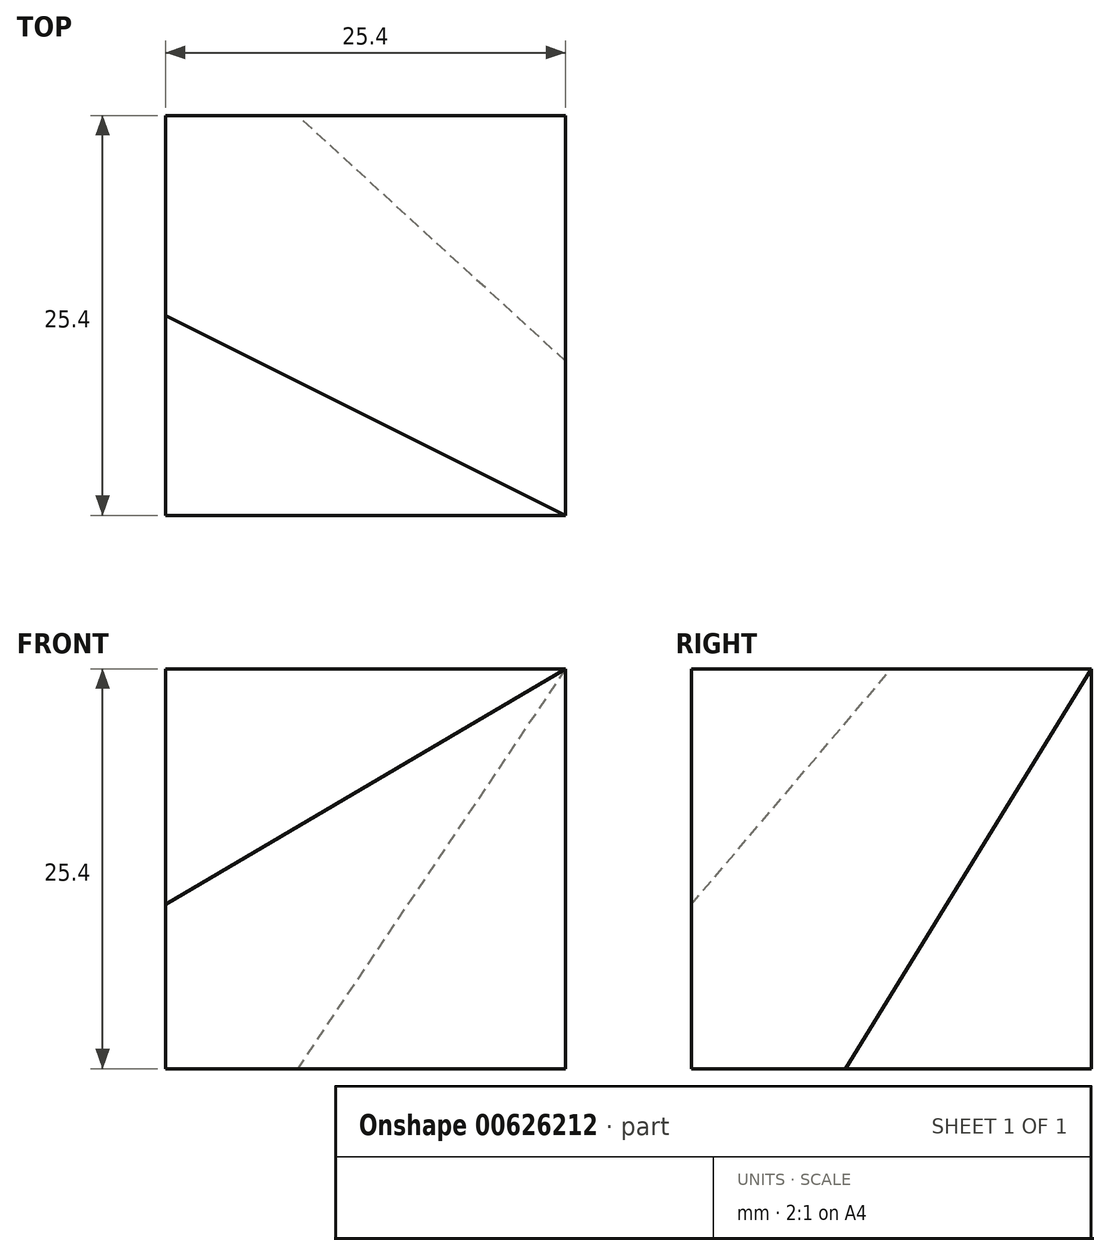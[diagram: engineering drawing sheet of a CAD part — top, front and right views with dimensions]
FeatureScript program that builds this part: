
annotation { "Feature Type Name" : "Feature", "Feature Type Description" : "" }
export const myFeature = defineFeature(function(context is Context, id is Id, definition is map)
    precondition{}
    {
        {
            var Q0;
            Q0=qCreatedBy(makeId("Top.planeOp"),FACE);
            var sketch = newSketch(context, id + "F0", { "sketchPlane" : qUnion([Q0])});
            skLineSegment(sketch, "E0.bottom", {"start": v(-12.7, 12.7) * mm, "end": v(12.7, 12.7) * mm});
            skLineSegment(sketch, "E0.top", {"start": v(-12.7, -12.7) * mm, "end": v(12.7, -12.7) * mm});
            skLineSegment(sketch, "E0.left", {"start": v(-12.7, 12.7) * mm, "end": v(-12.7, -12.7) * mm});
            skLineSegment(sketch, "E0.right", {"start": v(12.7, 12.7) * mm, "end": v(12.7, -12.7) * mm});
            skPoint(sketch, "E0.middle", {"position": v(0, 0) * mm});
            skSolve(sketch);
        }
        {
            var Q0;
            Q0 = qSketchRegion(id + "F0", true);
            extrude(context, id + "F1", {"entities" : qUnion([Q0]), "depth" : 25.4 * mm, "offsetDistance" : 25.4 * mm});
        }
        {
            var Q0;
            Q0=makeQuery(id+"F1.opExtrude","SWEPT_FACE",FACE,{"disambiguationData":[OSD([sQuery(id+"F0.wireOp",EDGE,"E0.left")])]});
            var sketch = newSketch(context, id + "F2", { "sketchPlane" : qUnion([Q0])});
            skLineSegment(sketch, "E1", {"start": v(-3.1, 25.4) * mm, "end": v(12.7, 10.44) * mm});
            skSolve(sketch);
        }
        {
            var Q0;
            Q0=makeQuery(id+"F1.opExtrude","CAP_EDGE",EDGE,{"disambiguationData":[OSD([sQuery(id+"F0.wireOp",EDGE,"E0.left")])],"isStart":false});
            cPoint(context, id + "F3", {"entities" : qUnion([Q0]), "parameter" : 0.5});
        }
        {
            var Q0;
            Q0 = qCreatedBy(id + "F3" ,VERTEX);
            var Q1;
            Q1=sQuery(id+"F2.wireOp",VERTEX,"E1.end");
            var Q2;
            Q2=makeQuery(id+"F1.opExtrude","CAP_VERTEX",VERTEX,{"disambiguationData":[OSD([sQuery(id+"F0.wireOp",EDGE,"E0.top"),sQuery(id+"F0.wireOp",EDGE,"E0.right")])],"isStart":false});
            cPlane(context, id + "F4", {"entities" : qUnion([Q0, Q1, Q2]), "cplaneType" : CPlaneType.THREE_POINT, "offset" : 25.4 * mm, "width" : 152.4 * mm, "height" : 152.4 * mm});
        }
        {
            var Q0;
            Q0=qCreatedBy(id+"F4.planeOp",FACE);
            var sketch = newSketch(context, id + "F5", { "sketchPlane" : qUnion([Q0])});
            skLineSegment(sketch, "E2.bottom", {"start": v(-23.97, -19.84) * mm, "end": v(63.45, -19.84) * mm});
            skLineSegment(sketch, "E2.top", {"start": v(-23.97, 113.8) * mm, "end": v(63.45, 113.8) * mm});
            skLineSegment(sketch, "E2.left", {"start": v(-23.97, -19.84) * mm, "end": v(-23.97, 113.8) * mm});
            skLineSegment(sketch, "E2.right", {"start": v(63.45, -19.84) * mm, "end": v(63.45, 113.8) * mm});
            skPoint(sketch, "E2.middle", {"position": v(19.74, 46.98) * mm});
            skSolve(sketch);
        }
        {
            var Q0;
            Q0 = qSketchRegion(id + "F5", true);
            extrude(context, id + "F6", {"entities" : qUnion([Q0]), "operationType" : NewBodyOperationType.REMOVE, "oppositeDirection" : true, "depth" : 25.4 * mm, "offsetDistance" : 25.4 * mm});
        }
        {
            var Q0;
            Q0=makeQuery(id+"F1.opExtrude","CAP_FACE",FACE,{"disambiguationData":[OSD([sQuery(id+"F0.wireOp",EDGE,"E0.bottom"),sQuery(id+"F0.wireOp",EDGE,"E0.top"),sQuery(id+"F0.wireOp",EDGE,"E0.left"),sQuery(id+"F0.wireOp",EDGE,"E0.right")])],"isStart":true});
            var sketch = newSketch(context, id + "F7", { "sketchPlane" : qUnion([Q0])});
            skLineSegment(sketch, "E3", {"start": v(-4.32, -12.7) * mm, "end": v(12.7, 2.92) * mm});
            skSolve(sketch);
        }
        {
            var Q0;
            Q0=sQuery(id+"F7.wireOp",VERTEX,"E3.start");
            var Q1;
            Q1=sQuery(id+"F7.wireOp",VERTEX,"E3.end");
            var Q2;
            Q2=makeQuery(id+"F1.opExtrude","CAP_VERTEX",VERTEX,{"disambiguationData":[OSD([sQuery(id+"F0.wireOp",EDGE,"E0.bottom"),sQuery(id+"F0.wireOp",EDGE,"E0.right")])],"isStart":false});
            cPlane(context, id + "F8", {"entities" : qUnion([Q0, Q1, Q2]), "cplaneType" : CPlaneType.THREE_POINT, "offset" : 25.4 * mm, "width" : 152.4 * mm, "height" : 152.4 * mm});
        }
        {
            var Q0;
            Q0=qCreatedBy(id+"F8.planeOp",FACE);
            var sketch = newSketch(context, id + "F9", { "sketchPlane" : qUnion([Q0])});
            skLineSegment(sketch, "E4.bottom", {"start": v(32.78, -34.36) * mm, "end": v(-67.33, -34.36) * mm});
            skLineSegment(sketch, "E4.top", {"start": v(32.78, 189.38) * mm, "end": v(-67.33, 189.38) * mm});
            skLineSegment(sketch, "E4.left", {"start": v(32.78, -34.36) * mm, "end": v(32.78, 189.38) * mm});
            skLineSegment(sketch, "E4.right", {"start": v(-67.33, -34.36) * mm, "end": v(-67.33, 189.38) * mm});
            skPoint(sketch, "E4.middle", {"position": v(-17.28, 77.51) * mm});
            skSolve(sketch);
        }
        {
            var Q0;
            Q0 = qSketchRegion(id + "F9", true);
            extrude(context, id + "F10", {"entities" : qUnion([Q0]), "operationType" : NewBodyOperationType.REMOVE, "depth" : 25.4 * mm, "offsetDistance" : 25.4 * mm});
        }
    });
